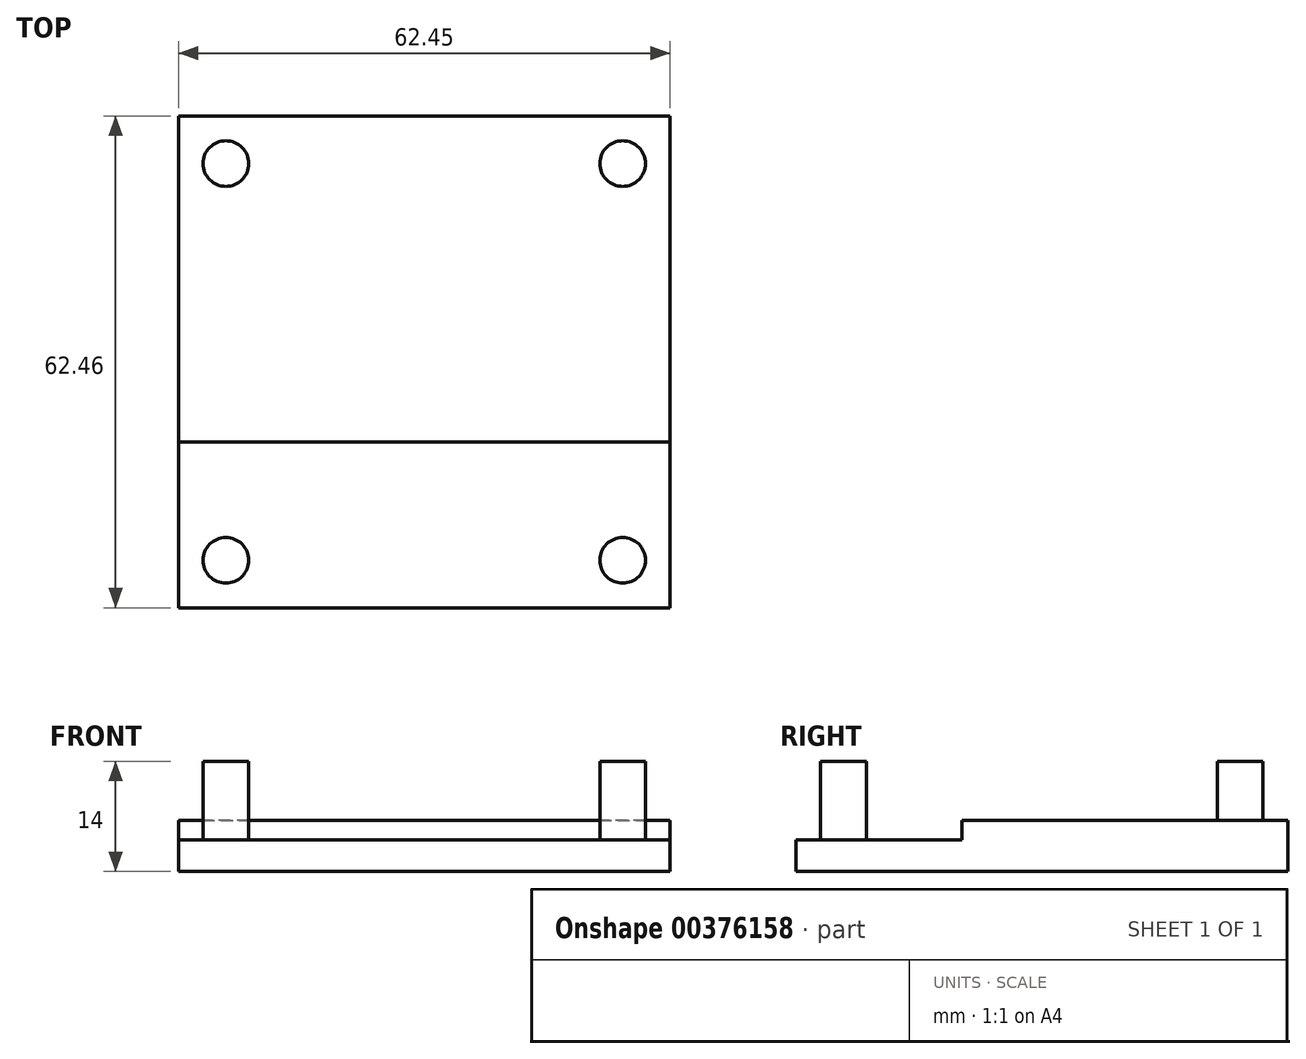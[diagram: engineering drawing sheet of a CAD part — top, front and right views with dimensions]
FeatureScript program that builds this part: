
annotation { "Feature Type Name" : "Feature", "Feature Type Description" : "" }
export const myFeature = defineFeature(function(context is Context, id is Id, definition is map)
    precondition{}
    {
        {
            var Q0;
            Q0=qCreatedBy(makeId("Top.planeOp"),FACE);
            var sketch = newSketch(context, id + "F0", { "sketchPlane" : qUnion([Q0])});
            skLineSegment(sketch, "E0.bottom", {"start": v(0, 0) * mm, "end": v(62.45, 0) * mm});
            skLineSegment(sketch, "E0.top", {"start": v(0, 62.46) * mm, "end": v(62.45, 62.46) * mm});
            skLineSegment(sketch, "E0.left", {"start": v(0, 0) * mm, "end": v(0, 62.46) * mm});
            skLineSegment(sketch, "E0.right", {"start": v(62.45, 0) * mm, "end": v(62.45, 62.46) * mm});
            skSolve(sketch);
        }
        {
            var Q0;
            Q0=makeQuery(id+"F0.imprint","IMPRINT",FACE,{"disambiguationData":[TD([[makeQuery(id+"F0.imprint","IMPRINT",EDGE,{"derivedFrom":sQuery(id+"F0.wireOp",EDGE,"E0.bottom")}),1.0]])]});
            extrude(context, id + "F1", {"entities" : qUnion([Q0]), "oppositeDirection" : true, "depth" : 4 * mm});
        }
        {
            var Q0;
            Q0=makeQuery(id+"F1.opExtrude","CAP_FACE",FACE,{"disambiguationData":[OSD([sQuery(id+"F0.wireOp",EDGE,"E0.bottom"),sQuery(id+"F0.wireOp",EDGE,"E0.top"),sQuery(id+"F0.wireOp",EDGE,"E0.left"),sQuery(id+"F0.wireOp",EDGE,"E0.right")])],"isStart":true});
            var sketch = newSketch(context, id + "F2", { "sketchPlane" : qUnion([Q0])});
            skCircle(sketch, "E1", {"center": v(6.03, 6.03) * mm, "radius": 2.9 * mm});
            skCircle(sketch, "E2", {"center": v(56.43, 6.03) * mm, "radius": 2.9 * mm});
            skSolve(sketch);
        }
        {
            var Q0;
            Q0=makeQuery(id+"F2.imprint","IMPRINT",FACE,{"disambiguationData":[TD([[makeQuery(id+"F2.imprint","IMPRINT",EDGE,{"derivedFrom":sQuery(id+"F2.wireOp",EDGE,"E1")}),-1.0]])]});
            var sketch = newSketch(context, id + "F3", { "sketchPlane" : qUnion([Q0])});
            skPoint(sketch, "E3", {"position": v(0, 0) * mm});
            skCircle(sketch, "E4", {"center": v(56.43, 56.43) * mm, "radius": 2.9 * mm});
            skCircle(sketch, "E5", {"center": v(6.03, 56.43) * mm, "radius": 2.9 * mm});
            skSolve(sketch);
        }
        {
            var Q0;
            Q0 = qSketchRegion(id + "F2", true);
            extrude(context, id + "F4", {"entities" : qUnion([Q0]), "operationType" : NewBodyOperationType.ADD, "depth" : 10 * mm});
        }
        {
            var Q0;
            Q0 = qSketchRegion(id + "F3", true);
            extrude(context, id + "F5", {"entities" : qUnion([Q0]), "operationType" : NewBodyOperationType.ADD, "depth" : 10 * mm});
        }
        {
            var Q0;
            Q0=makeQuery(id+"F1.opExtrude","CAP_FACE",FACE,{"disambiguationData":[OSD([sQuery(id+"F0.wireOp",EDGE,"E0.bottom"),sQuery(id+"F0.wireOp",EDGE,"E0.top"),sQuery(id+"F0.wireOp",EDGE,"E0.left"),sQuery(id+"F0.wireOp",EDGE,"E0.right")])],"isStart":true});
            var sketch = newSketch(context, id + "F6", { "sketchPlane" : qUnion([Q0])});
            skLineSegment(sketch, "E6.top", {"start": v(0, 21.08) * mm, "end": v(62.45, 21.08) * mm});
            skLineSegment(sketch, "E7.top", {"start": v(0, 62.46) * mm, "end": v(62.45, 62.46) * mm});
            skLineSegment(sketch, "E7.left", {"start": v(0, 21.08) * mm, "end": v(0, 62.46) * mm});
            skLineSegment(sketch, "E7.right", {"start": v(62.45, 21.08) * mm, "end": v(62.45, 62.46) * mm});
            skSolve(sketch);
        }
        {
            var Q0;
            Q0=makeQuery(id+"F6.imprint","IMPRINT",FACE,{"disambiguationData":[TD([[makeQuery(id+"F6.imprint","IMPRINT",EDGE,{"derivedFrom":sQuery(id+"F6.wireOp",EDGE,"E6.top")}),1.0]])]});
            extrude(context, id + "F7", {"entities" : qUnion([Q0]), "operationType" : NewBodyOperationType.ADD, "depth" : 2.5 * mm});
        }
    });
